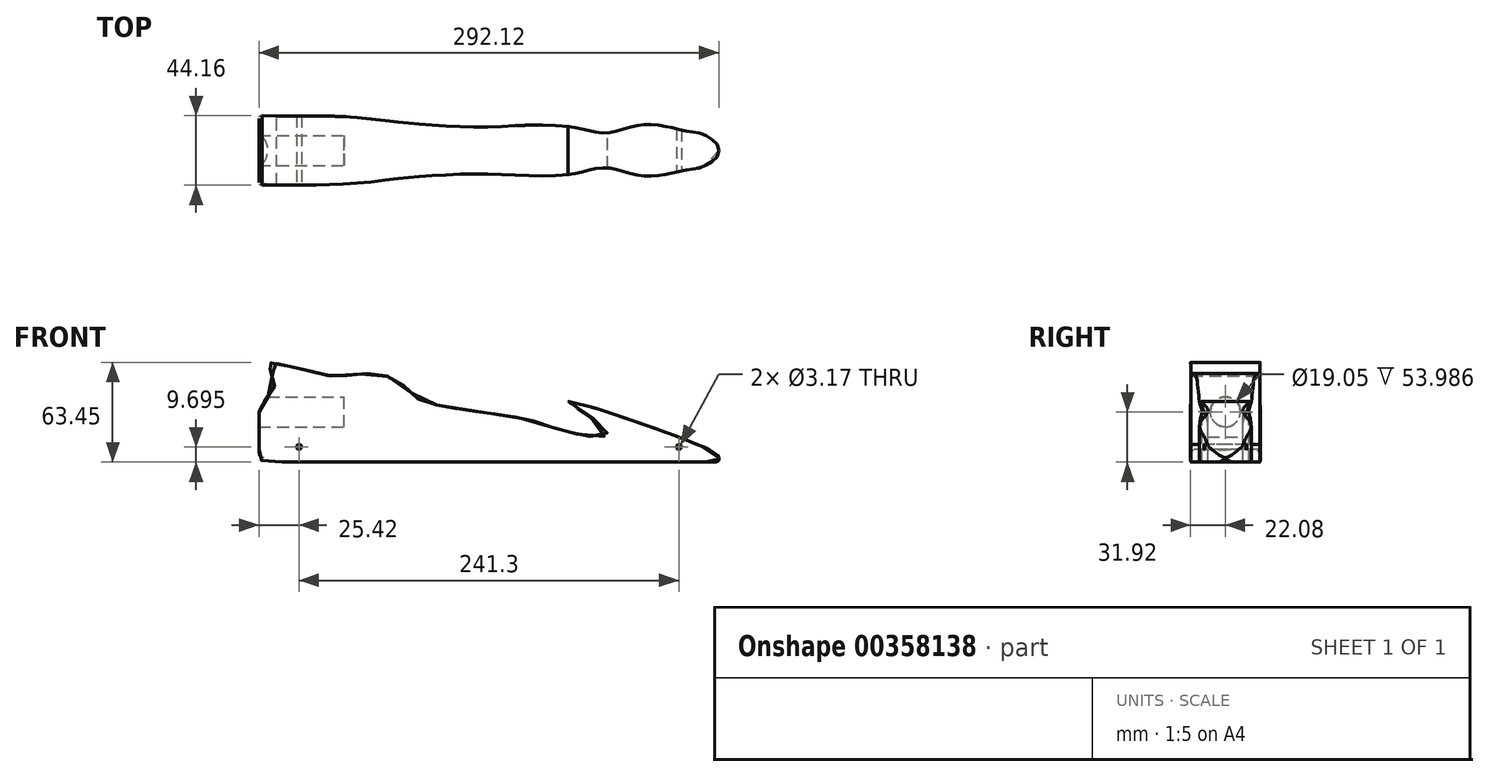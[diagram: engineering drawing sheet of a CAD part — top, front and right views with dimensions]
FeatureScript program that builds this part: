
annotation { "Feature Type Name" : "Feature", "Feature Type Description" : "" }
export const myFeature = defineFeature(function(context is Context, id is Id, definition is map)
    precondition{}
    {
        {
            var Q0;
            Q0=qCreatedBy(makeId("Front.planeOp"),FACE);
            var sketch = newSketch(context, id + "F0", { "sketchPlane" : qUnion([Q0])});
            skLineSegment(sketch, "E0.bottom", {"start": v(-146.05, 31.75) * mm, "end": v(146.05, 31.75) * mm, "construction": true});
            skLineSegment(sketch, "E0.top", {"start": v(-146.05, -31.75) * mm, "end": v(146.05, -31.75) * mm, "construction": true});
            skLineSegment(sketch, "E0.right", {"start": v(146.05, 31.75) * mm, "end": v(146.05, -31.75) * mm, "construction": true});
            skFitSpline(sketch, "E1", {"points": [v(-146.05, -24.02) * mm, v(-146.05, 0) * mm, v(-135.23, 22.74) * mm, v(-144.08, 31.1) * mm, v(-119.22, 27.34) * mm, v(-98.13, 22.74) * mm, v(-75.98, 24.5) * mm, v(-59.15, 20.52) * mm, v(-51.18, 13.87) * mm, v(-45.42, 8.56) * mm, v(-35.84, 4.82) * mm, v(26.07, -5.25) * mm, v(42.88, -10.72) * mm, v(74.47, -15.05) * mm, v(68.04, -5.49) * mm, v(50.3, 6.61) * mm, v(132.56, -20.74) * mm, v(146.05, -29.22) * mm, v(145.59, -31.27) * mm, v(144.47, -31.75) * mm, v(115.4, -31.75) * mm, v(90.89, -31.75) * mm, v(68.29, -31.75) * mm, v(46.65, -31.75) * mm, v(0, -31.75) * mm, v(-4.11, -31.75) * mm, v(-18.5, -31.75) * mm, v(-58.88, -31.75) * mm, v(-90.58, -31.75) * mm, v(-109.96, -31.75) * mm, v(-137.5, -31.75) * mm, v(-144.78, -30.62) * mm, v(-146.05, -24.02) * mm]});
            skLineSegment(sketch, "E2.bottom", {"start": v(-146.05, 9.52) * mm, "end": v(-95.25, 9.52) * mm, "construction": true});
            skLineSegment(sketch, "E2.top", {"start": v(-141.83, -9.52) * mm, "end": v(-95.25, -9.52) * mm, "construction": true});
            skLineSegment(sketch, "E2.right", {"start": v(-95.25, 9.52) * mm, "end": v(-95.25, -9.52) * mm, "construction": true});
            skLineSegment(sketch, "E3", {"start": v(-146.05, 31.75) * mm, "end": v(-146.05, -31.75) * mm, "construction": true});
            skPoint(sketch, "E4", {"position": v(0, 31.75) * mm});
            skSolve(sketch);
        }
        {
            var Q0;
            Q0=qCreatedBy(makeId("Top.planeOp"),FACE);
            var sketch = newSketch(context, id + "F1", { "sketchPlane" : qUnion([Q0])});
            skLineSegment(sketch, "E5.bottom", {"start": v(-146.05, 22.22) * mm, "end": v(146.05, 22.23) * mm, "construction": true});
            skLineSegment(sketch, "E5.top", {"start": v(-146.05, -22.23) * mm, "end": v(146.05, -22.22) * mm, "construction": true});
            skLineSegment(sketch, "E5.left", {"start": v(-146.05, 22.22) * mm, "end": v(-146.05, -22.23) * mm, "construction": true});
            skLineSegment(sketch, "E5.right", {"start": v(146.05, 22.22) * mm, "end": v(146.05, -22.22) * mm, "construction": true});
            skLineSegment(sketch, "E6", {"start": v(-146.05, 0) * mm, "end": v(146.05, 0) * mm, "construction": true});
            skFitSpline(sketch, "E7", {"points": [v(-146.05, 0) * mm, v(-146.04, 20) * mm, v(-145.68, 21.83) * mm, v(-141.76, 21.98) * mm, v(-93.94, 21.5) * mm, v(-55.24, 17.68) * mm, v(-13.2, 14.95) * mm, v(10.22, 15.4) * mm, v(52.72, 14.95) * mm, v(74.31, 11.08) * mm, v(99.09, 16.31) * mm, v(126.13, 12.22) * mm, v(135.68, 10.63) * mm, v(139.54, 8.36) * mm, v(146.05, 0) * mm], "startDerivative": vector(0, 335.54) * mm, "endDerivative": vector(0, -277.49) * mm});
            skFitSpline(sketch, "E8.MirrorCS", {"points": [v(-146.05, 0) * mm, v(-146.04, -20) * mm, v(-145.68, -21.83) * mm, v(-141.76, -21.98) * mm, v(-93.94, -21.5) * mm, v(-55.24, -17.68) * mm, v(-13.2, -14.95) * mm, v(10.22, -15.4) * mm, v(52.72, -14.95) * mm, v(74.31, -11.08) * mm, v(99.09, -16.31) * mm, v(126.13, -12.22) * mm, v(135.68, -10.63) * mm, v(139.54, -8.36) * mm, v(146.05, 0) * mm], "startDerivative": vector(0, -335.54) * mm, "endDerivative": vector(0, 277.49) * mm});
            skLineSegment(sketch, "E9.MirrorCS", {"start": v(-146.05, -22.23) * mm, "end": v(146.05, -22.23) * mm});
            skSolve(sketch);
        }
        {
            var Q0;
            Q0=qCreatedBy(makeId("Right.planeOp"),FACE);
            var sketch = newSketch(context, id + "F2", { "sketchPlane" : qUnion([Q0])});
            skCircle(sketch, "E10", {"center": v(0, 0) * mm, "radius": 9.53 * mm});
            skSolve(sketch);
        }
        {
            var Q0;
            Q0=qCreatedBy(makeId("Front.planeOp"),FACE);
            var sketch = newSketch(context, id + "F3", { "sketchPlane" : qUnion([Q0])});
            skCircle(sketch, "E11", {"center": v(-120.65, -22.22) * mm, "radius": 1.59 * mm});
            skCircle(sketch, "E12", {"center": v(120.65, -22.23) * mm, "radius": 1.59 * mm});
            skSolve(sketch);
        }
        {
            var Q0;
            Q0=qSketchRegion(id+"F0",true);
            extrude(context, id + "F4", {"entities" : qUnion([Q0]), "depth" : 44.45 * mm, "symmetric" : true});
        }
        {
            var Q0;
            Q0=qSketchRegion(id+"F1",true);
            extrude(context, id + "F5", {"entities" : qUnion([Q0]), "operationType" : NewBodyOperationType.INTERSECT, "endBound" : BoundingType.THROUGH_ALL, "oppositeDirection" : true, "depth" : 60.96 * mm, "hasSecondDirection" : true, "secondDirectionBound" : BoundingType.THROUGH_ALL, "secondDirectionOppositeDirection" : false, "secondDirectionDepth" : 25.4 * mm});
        }
        {
            var Q0;
            Q0=qSketchRegion(id+"F2",true);
            extrude(context, id + "F6", {"entities" : qUnion([Q0]), "operationType" : NewBodyOperationType.REMOVE, "oppositeDirection" : true, "depth" : 152.4 * mm, "hasSecondDirection" : true, "secondDirectionOppositeDirection" : true, "secondDirectionDepth" : 92.07 * mm});
        }
        {
            var Q0;
            Q0=qSketchRegion(id+"F3",true);
            extrude(context, id + "F7", {"entities" : qUnion([Q0]), "operationType" : NewBodyOperationType.REMOVE, "oppositeDirection" : true, "depth" : 50.8 * mm, "symmetric" : true});
        }
    });
